# Revit family: PRE070013-FR
name_source: partatom
category: Accessoire de canalisation
revit_build: Autodesk Revit 2017 (Build: 20160225_1515(x64)
units: mm (PartAtom-declared; Revit-internal decimal feet)

## family parameters
Basée sur le plan de construction = Non
Cote de connecteur circulaire = Utiliser le diamètre
Couper avec des vides une fois chargée = Non
Partagée = Non
Toujours verticalement = Oui
Type d'élément = Normal

## types (1)
- 75391 PRESTO Sanifirst Mitigeur d'évier à bec orientable
    Adresse = 7, RUE RACINE - 92542 MONTROUGE CEDEX FRANCE
    Debit = 3 l/mn
    Description = Mitigeur d’évier monotrou sans vidage pour lave-mains, à poser sur table avec manette pleine. Bec extrudé lisse orientable Lg 225mm. Hauteur sous bec 140mm. Cartouche céramique Ø 40 multifonction : butée de limitation de température  avec 7 positions de réglage, double débit et réglage du débit maximum.  Robinetterie montée d’origine avec un mousseur M24X1. Flexibles SPEX M12X1, EP G’3/8, Lg 370mm. Fixation renforcée par une tige M8.
    Diamètre Nominal = 12 mm  [stored 0.0393701 ft]
    Fabricant = LES ROBINETS PRESTO S.A.
    Finition = Corps lisse, bec et organe de manœuvre en laiton poli chromé.
    Flux = 0.1 L/s
    Fonction = Hauteur sous bec : 140 mm
Saillie : 225 mm
Organe de manoeuvre : Manette pleine
Référence : 75391
    Garantie = 10 ans contre tout vice de fabrication
    Hauteur = 165 mm  [stored 0.541339 ft]
    LC = 18 mm
    Largeur = 47 mm  [stored 0.154199 ft]
    Lien CCTP = http://www.prestodatashare.com
    Lien fiche produit = http://www.prestodatashare.com
    Lien notice d'utilisation = http://www.prestodatashare.com
    Matériau = Laiton poli chromé
    Modèle = 75391 PRESTO Sanifirst Mitigeur d'évier à bec orientable
    PC = 28 mm
    Perte de charge = 0.0 Pa
    Polantis code = PRE070013
    Pression = 3 bar
    Profondeur = 260 mm  [stored 0.853018 ft]
    Raccordement = Flexibles SPEX  370 mm - M12 X 1 - EP G'3/8
    Reference = 75391
    URL = http://www.prestodatashare.com
    URL Fabricant = http://www.prestodatashare.com
    Variantes = 75391

note: [stored X ft] marks values corroborated as IEEE doubles in the binary element streams (Revit-internal decimal feet)
